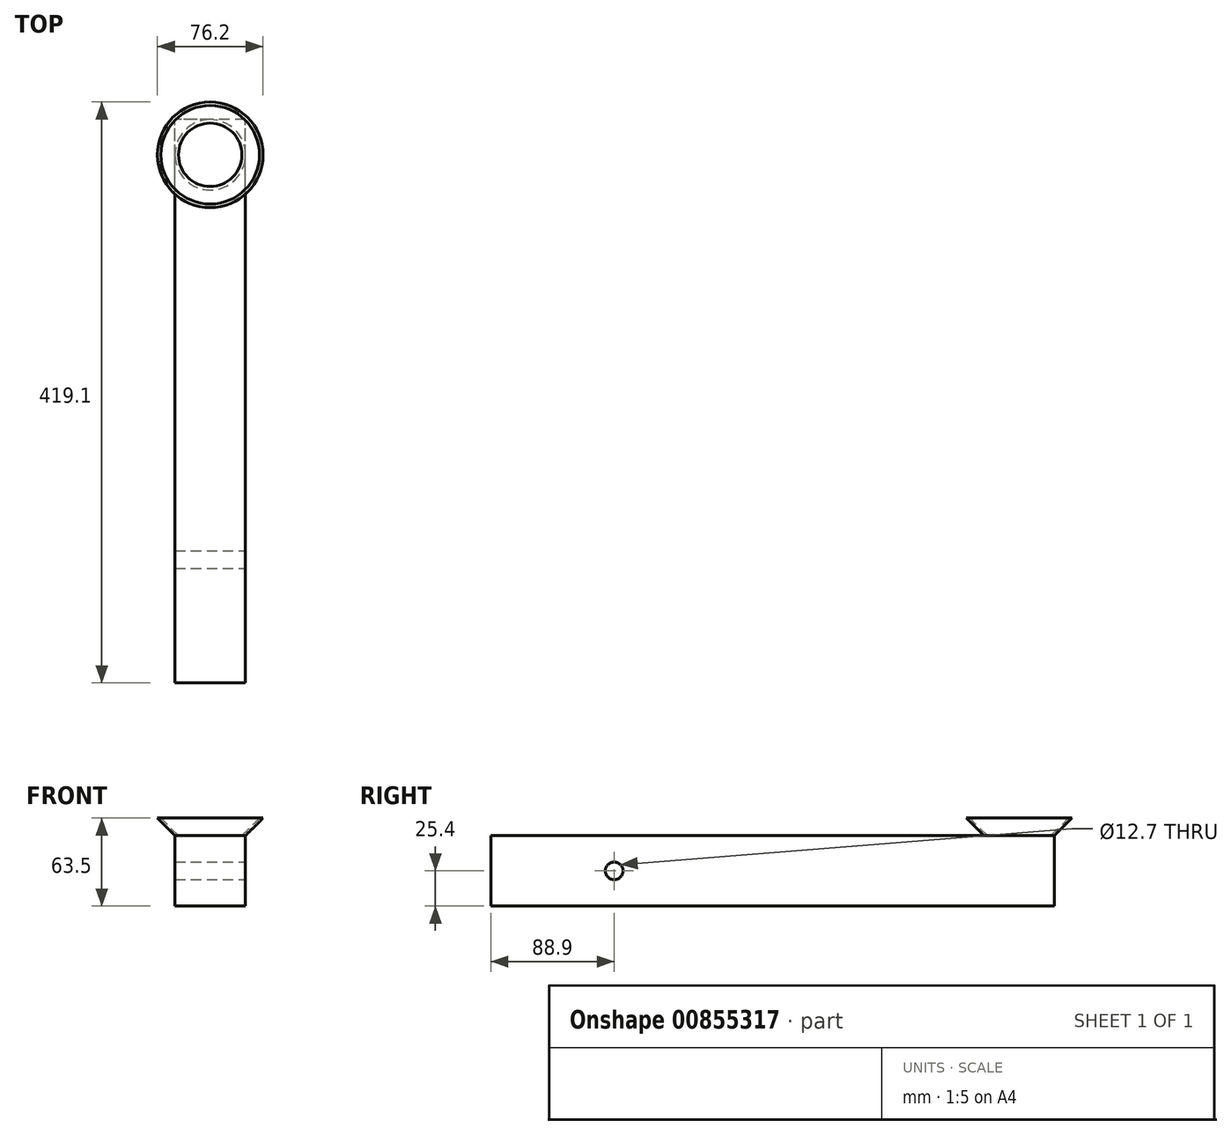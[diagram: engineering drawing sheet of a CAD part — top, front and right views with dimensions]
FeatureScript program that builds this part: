
annotation { "Feature Type Name" : "Feature", "Feature Type Description" : "" }
export const myFeature = defineFeature(function(context is Context, id is Id, definition is map)
    precondition{}
    {
        {
            var Q0;
            Q0=qCreatedBy(makeId("Top.planeOp"),FACE);
            var sketch = newSketch(context, id + "F0", { "sketchPlane" : qUnion([Q0])});
            skLineSegment(sketch, "E0.bottom", {"start": v(25.4, -203.2) * mm, "end": v(-25.4, -203.2) * mm});
            skLineSegment(sketch, "E0.top", {"start": v(25.4, 203.2) * mm, "end": v(-25.4, 203.2) * mm});
            skLineSegment(sketch, "E0.left", {"start": v(25.4, -203.2) * mm, "end": v(25.4, 203.2) * mm});
            skLineSegment(sketch, "E0.right", {"start": v(-25.4, -203.2) * mm, "end": v(-25.4, 203.2) * mm});
            skPoint(sketch, "E0.middle", {"position": v(0, 0) * mm});
            skSolve(sketch);
        }
        {
            var Q0;
            Q0 = qSketchRegion(id + "F0", true);
            extrude(context, id + "F1", {"entities" : qUnion([Q0]), "depth" : 50.8 * mm, "offsetDistance" : 25.4 * mm});
        }
        {
            var Q0;
            Q0=makeQuery(id+"F1.opExtrude","SWEPT_FACE",FACE,{"disambiguationData":[OSD([sQuery(id+"F0.wireOp",EDGE,"E0.left")])]});
            var sketch = newSketch(context, id + "F2", { "sketchPlane" : qUnion([Q0])});
            skCircle(sketch, "E1", {"center": v(-114.3, 25.4) * mm, "radius": 6.35 * mm});
            skPoint(sketch, "E1.centerSnap0", {"position": v(-203.2, 25.4) * mm});
            skSolve(sketch);
        }
        {
            var Q0;
            Q0 = qSketchRegion(id + "F2", true);
            extrude(context, id + "F3", {"entities" : qUnion([Q0]), "operationType" : NewBodyOperationType.REMOVE, "endBound" : BoundingType.THROUGH_ALL, "oppositeDirection" : true, "depth" : 25.4 * mm, "offsetDistance" : 25.4 * mm});
        }
        {
            var Q0;
            Q0=makeQuery(id+"F1.opExtrude","CAP_FACE",FACE,{"disambiguationData":[OSD([sQuery(id+"F0.wireOp",EDGE,"E0.bottom"),sQuery(id+"F0.wireOp",EDGE,"E0.top"),sQuery(id+"F0.wireOp",EDGE,"E0.left"),sQuery(id+"F0.wireOp",EDGE,"E0.right")])],"isStart":false});
            var sketch = newSketch(context, id + "F4", { "sketchPlane" : qUnion([Q0])});
            skCircle(sketch, "E2", {"center": v(0, 177.8) * mm, "radius": 25.4 * mm});
            skSolve(sketch);
        }
        {
            var Q0;
            {var subQ0=sQuery(id+"F4.wireOp",EDGE,"E2");var subQ1=makeQuery(id+"F4.imprint","INTERSECT",VERTEX,{"derivedFrom":[makeQuery(id+"F1.opExtrude","CAP_EDGE",EDGE,{"disambiguationData":[OSD([sQuery(id+"F0.wireOp",EDGE,"E0.top")])],"isStart":false}),subQ0]});Q0=makeQuery(id+"F4.imprint","IMPRINT",FACE,{"disambiguationData":[TD([[makeQuery(id+"F4.imprint","IMPRINT",EDGE,{"disambiguationData":[TD([[subQ1,1.0]])],"derivedFrom":subQ0}),1.0]])]});}
            cPlane(context, id + "F5", {"entities" : qUnion([Q0]), "cplaneType" : CPlaneType.OFFSET, "offset" : 12.7 * mm, "width" : 152.4 * mm, "height" : 152.4 * mm});
        }
        {
            var Q0;
            Q0=qCreatedBy(id+"F5.planeOp",FACE);
            var sketch = newSketch(context, id + "F6", { "sketchPlane" : qUnion([Q0])});
            skCircle(sketch, "E3", {"center": v(0, 177.8) * mm, "radius": 38.1 * mm});
            skSolve(sketch);
        }
        {
            var Q1;
            {var subQ0=sQuery(id+"F4.wireOp",EDGE,"E2");var subQ1=makeQuery(id+"F4.imprint","INTERSECT",VERTEX,{"derivedFrom":[makeQuery(id+"F1.opExtrude","CAP_EDGE",EDGE,{"disambiguationData":[OSD([sQuery(id+"F0.wireOp",EDGE,"E0.top")])],"isStart":false}),subQ0]});Q1=makeQuery(id+"F4.imprint","IMPRINT",FACE,{"disambiguationData":[TD([[makeQuery(id+"F4.imprint","IMPRINT",EDGE,{"disambiguationData":[TD([[subQ1,1.0]])],"derivedFrom":subQ0}),1.0]])]});}
            var Q2;
            Q2=makeQuery(id+"F6.imprint","IMPRINT",FACE,{"disambiguationData":[TD([[makeQuery(id+"F6.imprint","IMPRINT",EDGE,{"derivedFrom":sQuery(id+"F6.wireOp",EDGE,"E3")}),1.0]])]});
            loft(context, id + "F7", {"operationType" : NewBodyOperationType.ADD, "sheetProfilesArray" : [{ "sheetProfileEntities" : qUnion([Q1]) }, { "sheetProfileEntities" : qUnion([Q2]) }]});
        }
        {
            var Q0;
            {var subQ5=makeQuery(id+"F1.opExtrude","CAP_EDGE",EDGE,{"disambiguationData":[OSD([sQuery(id+"F0.wireOp",EDGE,"E0.bottom")])],"isStart":false});Q0=makeQuery(id+"F4.imprint","IMPRINT",FACE,{"disambiguationData":[TD([[makeQuery(id+"F4.imprint","IMPRINT",EDGE,{"derivedFrom":subQ5}),-1.0]])]});}
            var sketch = newSketch(context, id + "F8", { "sketchPlane" : qUnion([Q0])});
            skCircle(sketch, "E4", {"center": v(0, 177.8) * mm, "radius": 22.86 * mm});
            skSolve(sketch);
        }
        {
            var Q0;
            Q0=makeQuery(id+"F6.imprint","IMPRINT",FACE,{"disambiguationData":[TD([[makeQuery(id+"F6.imprint","IMPRINT",EDGE,{"derivedFrom":sQuery(id+"F6.wireOp",EDGE,"E3")}),1.0]])]});
            var sketch = newSketch(context, id + "F9", { "sketchPlane" : qUnion([Q0])});
            skCircle(sketch, "E5", {"center": v(0, 177.8) * mm, "radius": 35.56 * mm});
            skSolve(sketch);
        }
        {
            var Q1;
            Q1 = qSketchRegion(id + "F9", true);
            var Q2;
            Q2 = qSketchRegion(id + "F8", true);
            loft(context, id + "F10", {"operationType" : NewBodyOperationType.REMOVE, "sheetProfilesArray" : [{ "sheetProfileEntities" : qUnion([Q1]) }, { "sheetProfileEntities" : qUnion([Q2]) }]});
        }
    });
